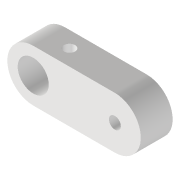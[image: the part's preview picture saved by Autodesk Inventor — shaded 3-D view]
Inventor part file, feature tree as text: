
AUTODESK INVENTOR PART (.ipt)
format: ipt  version: 2022 (Build 260153000, 153)  size: 113,152 bytes
history: native  units: mm
features: extrude x3, sketch x3, other x2, reference x1
ambient origin geometry x8: Origin, YZ Plane, XZ Plane, XY Plane, X Axis, Y Axis, Z Axis, Center Point
bodies: Volumenkörper1 (feature_tree)
feature tree (9):
  extrude  "Extrusion1"  Depth=7.8mm
  extrude  "Extrusion2"  Depth=8.0mm TaperAngle=0.0deg
  extrude  "Extrusion3"  Depth=6.0mm TaperAngle=0.0deg
  sketch  "Skizze1"  dims[d0=3.0mm d1=7.8mm]
  reference  "Referenz1"
  sketch  "Skizze2"  dims[d2=13.0mm d3=8.0mm d4=0.0mm]
  sketch  "Skizze3"  dims[d5=7.0mm d6=6.0mm d7=0.0mm d8=2.8mm d9=0.0mm d10=0.0mm]
  other  "Assembly_HoliSheet_v5.iam"
  other  "00_NEMA8:1"
